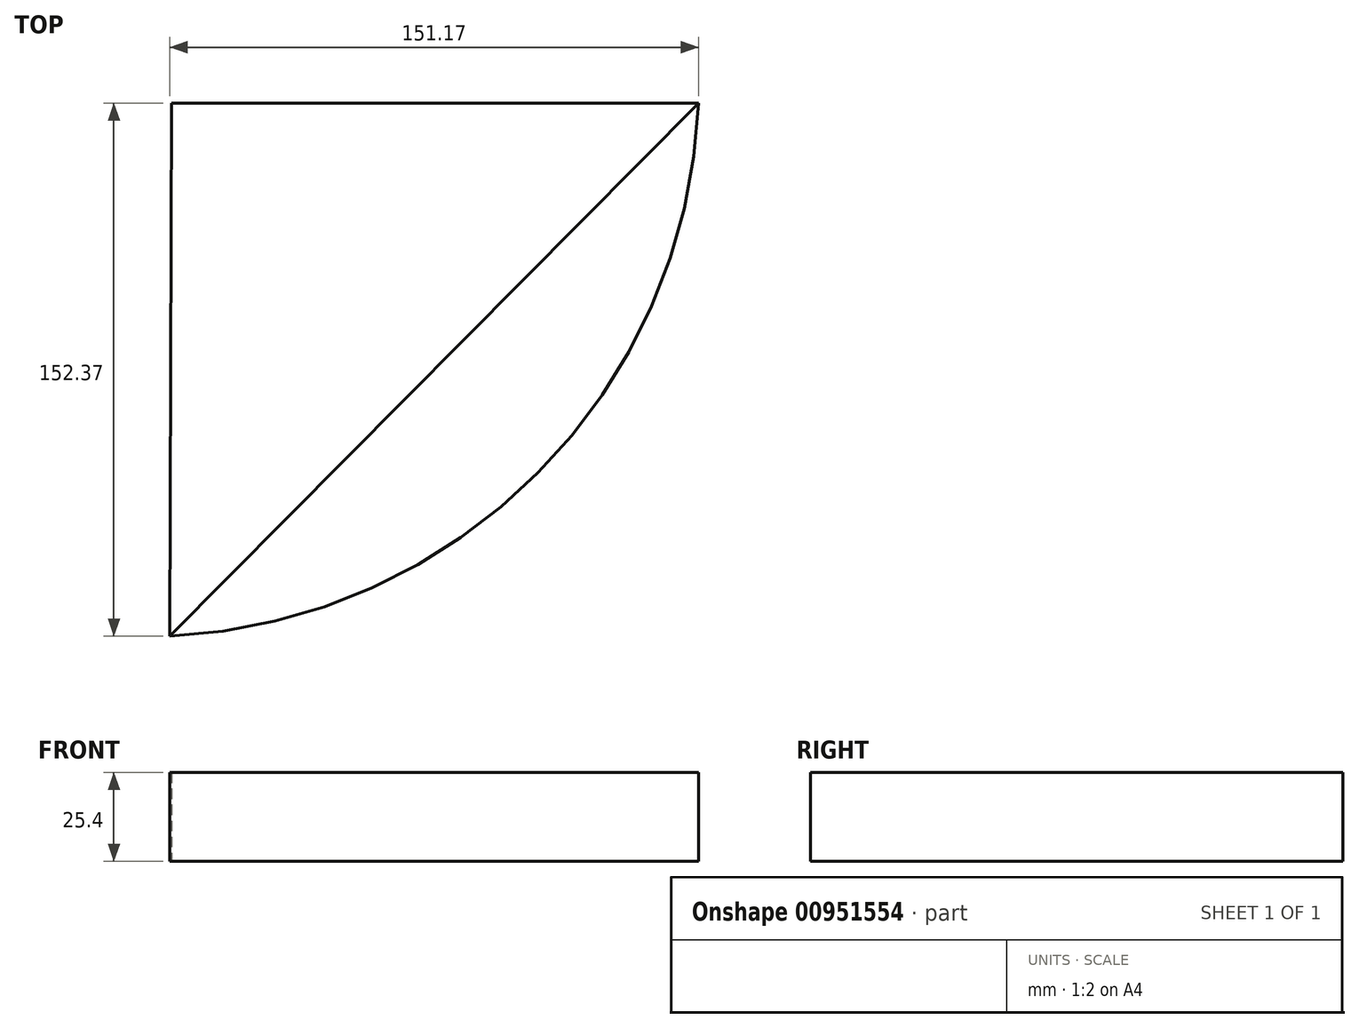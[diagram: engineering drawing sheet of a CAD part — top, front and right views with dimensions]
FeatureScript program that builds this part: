
annotation { "Feature Type Name" : "Feature", "Feature Type Description" : "" }
export const myFeature = defineFeature(function(context is Context, id is Id, definition is map)
    precondition{}
    {
        {
            var Q0;
            Q0=qCreatedBy(makeId("Top.planeOp"),FACE);
            var sketch = newSketch(context, id + "F0", { "sketchPlane" : qUnion([Q0])});
            skLineSegment(sketch, "E0", {"start": v(-75.55, 75.73) * mm, "end": v(75.13, 75.73) * mm});
            skLineSegment(sketch, "E1", {"start": v(75.13, 75.73) * mm, "end": v(-76.04, -76.64) * mm});
            skLineSegment(sketch, "E2", {"start": v(-76.04, -76.64) * mm, "end": v(-75.55, 75.73) * mm});
            skSolve(sketch);
        }
        {
            var Q0;
            Q0=makeQuery(id+"F0.imprint","IMPRINT",FACE,{"disambiguationData":[TD([[makeQuery(id+"F0.imprint","IMPRINT",EDGE,{"derivedFrom":sQuery(id+"F0.wireOp",EDGE,"E0")}),-1.0]])]});
            var sketch = newSketch(context, id + "F1", { "sketchPlane" : qUnion([Q0])});
            skArc(sketch, "E3", {"start": v(-76.94, -77.24) * mm, "mid": v(38.12, -39.55) * mm, "end": v(75.13, 75.74) * mm});
            skSolve(sketch);
        }
        {
            var Q0;
            Q0=makeQuery(id+"F1.imprint","IMPRINT",FACE,{"disambiguationData":[TD([[makeQuery(id+"F1.imprint","IMPRINT",EDGE,{"derivedFrom":makeQuery(id+"F0.imprint","IMPRINT",EDGE,{"derivedFrom":sQuery(id+"F0.wireOp",EDGE,"E0")})}),-1.0]])]});
            extrude(context, id + "F2", {"entities" : qUnion([Q0]), "depth" : 25.4 * mm, "offsetDistance" : 25.4 * mm});
        }
        {
            var Q0;
            Q0=makeQuery(id+"F2.opExtrude","CAP_FACE",FACE,{"disambiguationData":[OSD([sQuery(id+"F0.wireOp",EDGE,"E0"),sQuery(id+"F0.wireOp",EDGE,"E1"),sQuery(id+"F0.wireOp",EDGE,"E2")])],"isStart":false});
            var sketch = newSketch(context, id + "F3", { "sketchPlane" : qUnion([Q0])});
            skArc(sketch, "E4", {"start": v(-76.04, -76.64) * mm, "mid": v(29.22, -29.9) * mm, "end": v(75.13, 75.73) * mm});
            skSolve(sketch);
        }
        {
            var Q0;
            Q0=makeQuery(id+"F3.imprint","IMPRINT",FACE,{"disambiguationData":[TD([[makeQuery(id+"F3.imprint","IMPRINT",EDGE,{"derivedFrom":sQuery(id+"F3.wireOp",EDGE,"E4")}),1.0]])]});
            extrude(context, id + "F4", {"entities" : qUnion([Q0]), "oppositeDirection" : true, "depth" : 25.4 * mm, "offsetDistance" : 25.4 * mm});
        }
    });
